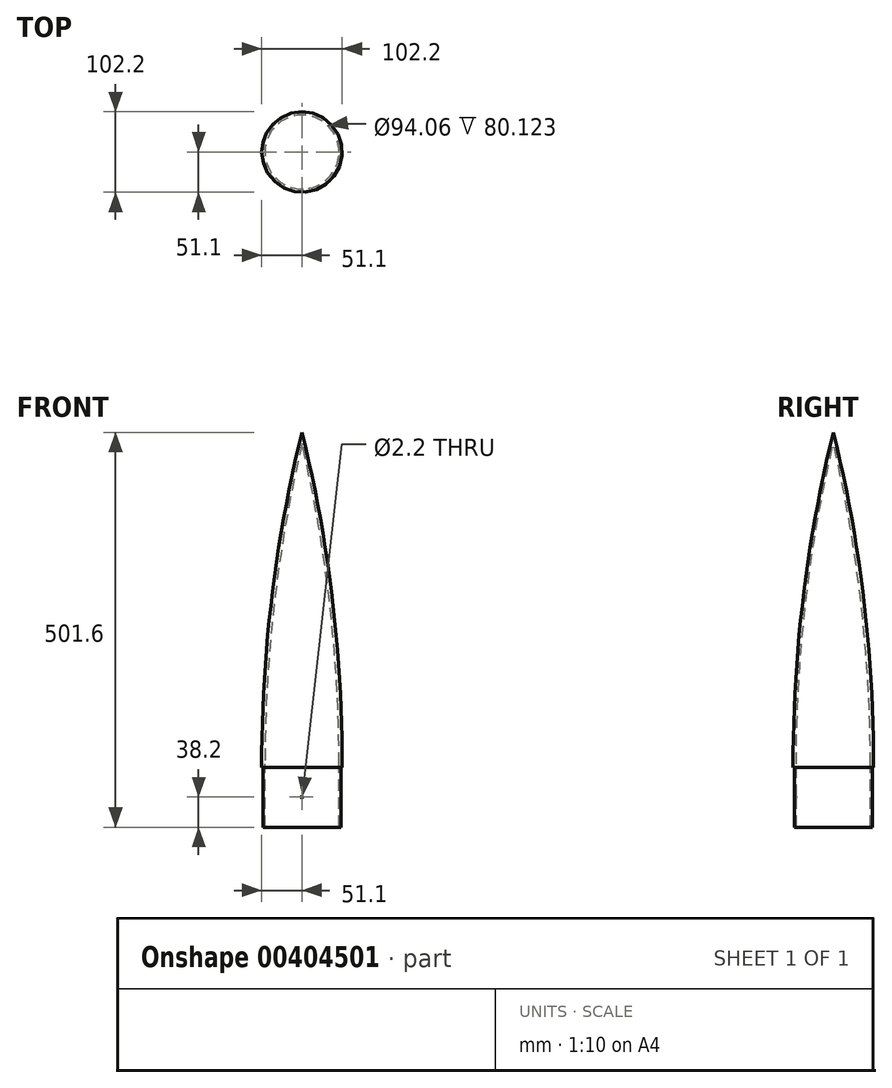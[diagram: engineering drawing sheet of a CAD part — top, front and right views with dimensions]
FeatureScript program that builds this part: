
annotation { "Feature Type Name" : "Feature", "Feature Type Description" : "" }
export const myFeature = defineFeature(function(context is Context, id is Id, definition is map)
    precondition{}
    {
        {
            var Q0;
            Q0=qCreatedBy(makeId("Front.planeOp"),FACE);
            var sketch = newSketch(context, id + "F0", { "sketchPlane" : qUnion([Q0])});
            skLineSegment(sketch, "E0", {"start": v(-49.53, 0) * mm, "end": v(-49.53, 76.2) * mm});
            skLineSegment(sketch, "E1", {"start": v(-49.53, 76.2) * mm, "end": v(-51.1, 76.2) * mm});
            skPoint(sketch, "E2", {"position": v(0, 501.6) * mm});
            skPoint(sketch, "E3", {"position": v(-49.53, 76.2) * mm});
            skArc(sketch, "E4", {"start": v(0, 501.6) * mm, "mid": v(-38.49, 290.45) * mm, "end": v(-51.1, 76.2) * mm});
            skLineSegment(sketch, "E5", {"start": v(-49.53, 0) * mm, "end": v(-47.03, 0) * mm});
            skPoint(sketch, "E6", {"position": v(0, 487.51) * mm});
            skLineSegment(sketch, "E7", {"start": v(-47.03, 80.12) * mm, "end": v(-47.03, 0) * mm});
            skArc(sketch, "E8", {"start": v(0, 487.51) * mm, "mid": v(-35.18, 285.16) * mm, "end": v(-47.03, 80.12) * mm});
            skLineSegment(sketch, "E9", {"start": v(0, 501.6) * mm, "end": v(0, 487.51) * mm});
            skSolve(sketch);
        }
        {
            var Q0;
            Q0=qCreatedBy(makeId("Front.planeOp"),FACE);
            var sketch = newSketch(context, id + "F1", { "sketchPlane" : qUnion([Q0])});
            skLineSegment(sketch, "E10", {"start": v(0, 14.17) * mm, "end": v(0, -34.8) * mm});
            skSolve(sketch);
        }
        {
            var Q0;
            Q0=makeQuery(id+"F0.imprint","IMPRINT",FACE,{"disambiguationData":[TD([[makeQuery(id+"F0.imprint","IMPRINT",EDGE,{"derivedFrom":sQuery(id+"F0.wireOp",EDGE,"E0")}),-1.0]])]});
            var Q1;
            Q1=sQuery(id+"F1.wireOp",EDGE,"E10");
            revolve(context, id + "F2", {"entities" : qUnion([Q0]), "axis" : qUnion([Q1]), "revolveType" : RevolveType.FULL});
        }
        {
            var Q0;
            Q0=qCreatedBy(makeId("Front.planeOp"),FACE);
            var sketch = newSketch(context, id + "F3", { "sketchPlane" : qUnion([Q0])});
            skPoint(sketch, "E11", {"position": v(0, 38.2) * mm});
            skSolve(sketch);
        }
        {
            var Q0;
            Q0=sQuery(id+"F3.wireOp",VERTEX,"E11");
            var Q1;
            Q1=makeQuery(id+"F2.opRevolve","SWEPT_BODY",BODY,{"disambiguationData":[OSD([sQuery(id+"F0.wireOp",EDGE,"E0"),sQuery(id+"F0.wireOp",EDGE,"E1"),sQuery(id+"F0.wireOp",EDGE,"E4"),sQuery(id+"F0.wireOp",EDGE,"E5"),sQuery(id+"F0.wireOp",EDGE,"E7"),sQuery(id+"F0.wireOp",EDGE,"E8"),sQuery(id+"F0.wireOp",EDGE,"E9")])]});
            hole(context, id + "F4", {"style" : HoleStyle.SIMPLE, "endStyle" : HoleEndStyle.THROUGH, "oppositeDirection" : true, "holeDiameter" : 2.2 * mm, "majorDiameter" : 5 * mm, "isTappedThrough" : true, "tappedDepth" : 12 * mm, "tapClearance" : 3, "startFromSketch" : true, "locations" : qUnion([Q0]), "scope" : qUnion([Q1])});
        }
    });
